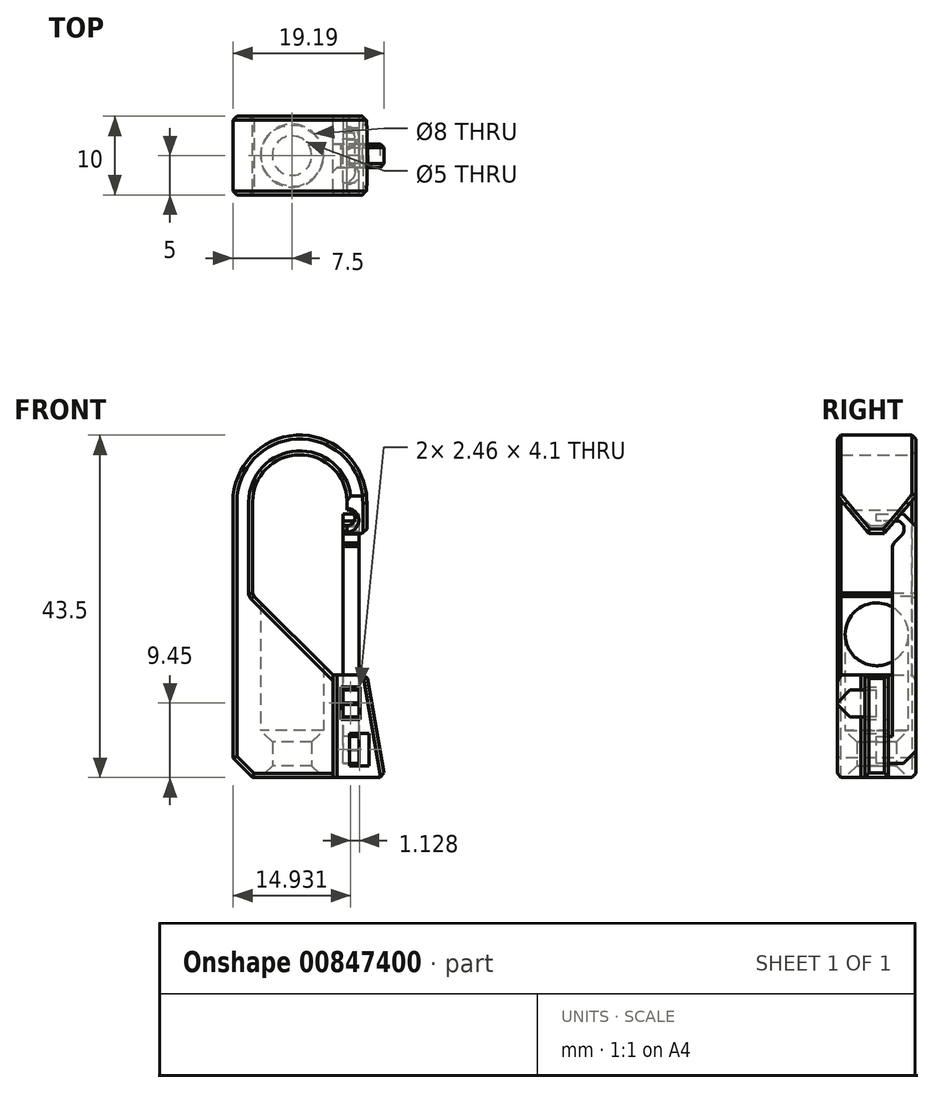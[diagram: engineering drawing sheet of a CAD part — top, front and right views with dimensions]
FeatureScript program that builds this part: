
annotation { "Feature Type Name" : "Feature", "Feature Type Description" : "" }
export const myFeature = defineFeature(function(context is Context, id is Id, definition is map)
    precondition{}
    {
        {
            var Q0;
            Q0=qCreatedBy(makeId("Top.planeOp"),FACE);
            var sketch = newSketch(context, id + "F0", { "sketchPlane" : qUnion([Q0])});
            skCircle(sketch, "E0", {"center": v(-1, -1.5) * mm, "radius": 4 * mm});
            skLineSegment(sketch, "E1.bottom", {"start": v(-8.5, 3.5) * mm, "end": v(8.5, 3.5) * mm});
            skLineSegment(sketch, "E1.top", {"start": v(-8.5, -6.5) * mm, "end": v(8.5, -6.5) * mm});
            skLineSegment(sketch, "E1.left", {"start": v(-8.5, 3.5) * mm, "end": v(-8.5, -6.5) * mm});
            skLineSegment(sketch, "E1.right", {"start": v(8.5, 3.5) * mm, "end": v(8.5, -6.5) * mm});
            skPoint(sketch, "E1.middle", {"position": v(0, -1.5) * mm});
            skCircle(sketch, "E2", {"center": v(-1, -1.5) * mm, "radius": 2.5 * mm});
            skSolve(sketch);
        }
        {
            var Q0;
            Q0=qCreatedBy(makeId("Front.planeOp"),FACE);
            cPlane(context, id + "F1", {"entities" : qUnion([Q0]), "cplaneType" : CPlaneType.OFFSET, "offset" : 3.5 * mm, "oppositeDirection" : true, "width" : 150 * mm, "height" : 150 * mm});
        }
        {
            var Q0;
            Q0=qCreatedBy(id+"F1.planeOp",FACE);
            var sketch = newSketch(context, id + "F2", { "sketchPlane" : qUnion([Q0])});
            skLineSegment(sketch, "E3", {"start": v(0, 0) * mm, "end": v(8.5, 0) * mm});
            skLineSegment(sketch, "E4.MirrorCS", {"start": v(0, 0) * mm, "end": v(-8.5, 0) * mm});
            skLineSegment(sketch, "E5", {"start": v(8.5, 0) * mm, "end": v(8.5, 13) * mm});
            skLineSegment(sketch, "E6", {"start": v(8.5, 13) * mm, "end": v(4.2, 13) * mm});
            skLineSegment(sketch, "E7", {"start": v(4.2, 13) * mm, "end": v(-6, 23.2) * mm});
            skLineSegment(sketch, "E8", {"start": v(-8.5, 0) * mm, "end": v(-8.5, 35) * mm});
            skLineSegment(sketch, "E9", {"start": v(-6, 23.2) * mm, "end": v(-6, 35) * mm});
            skLineSegment(sketch, "E10", {"start": v(-6, 35) * mm, "end": v(0, 35) * mm});
            skArc(sketch, "E11", {"start": v(8.5, 35) * mm, "mid": v(0, 43.5) * mm, "end": v(-8.5, 35) * mm});
            skArc(sketch, "E12", {"start": v(6, 35) * mm, "mid": v(0, 41) * mm, "end": v(-6, 35) * mm});
            skLineSegment(sketch, "E13", {"start": v(0, 35) * mm, "end": v(8.5, 35) * mm});
            skLineSegment(sketch, "E14", {"start": v(6, 35) * mm, "end": v(6, 31) * mm});
            skLineSegment(sketch, "E15.bottom", {"start": v(6, 31) * mm, "end": v(8.5, 31) * mm});
            skLineSegment(sketch, "E15.top", {"start": v(6, 35) * mm, "end": v(8.5, 35) * mm});
            skLineSegment(sketch, "E15.left", {"start": v(6, 31) * mm, "end": v(6, 35) * mm});
            skLineSegment(sketch, "E15.right", {"start": v(8.5, 31) * mm, "end": v(8.5, 35) * mm});
            skLineSegment(sketch, "E16", {"start": v(8.5, 13) * mm, "end": v(10.8, 0) * mm});
            skLineSegment(sketch, "E17", {"start": v(10.8, 0) * mm, "end": v(8.5, 0) * mm});
            skLineSegment(sketch, "E18", {"start": v(4.2, 13) * mm, "end": v(4.2, 0) * mm});
            skLineSegment(sketch, "E19.0", {"start": v(5.2, 12) * mm, "end": v(5.2, 0) * mm});
            skLineSegment(sketch, "E19.1", {"start": v(7.66, 12) * mm, "end": v(5.2, 12) * mm});
            skLineSegment(sketch, "E19.2", {"start": v(7.66, 12) * mm, "end": v(9.6, 1) * mm});
            skLineSegment(sketch, "E19.3", {"start": v(9.6, 1) * mm, "end": v(8.5, 1) * mm});
            skLineSegment(sketch, "E20", {"start": v(8.5, 1) * mm, "end": v(5.2, 1) * mm});
            skLineSegment(sketch, "E21", {"start": v(5.2, 12) * mm, "end": v(7.14, 1) * mm});
            skCircle(sketch, "E22", {"center": v(6, 33) * mm, "radius": 1 * mm});
            skLineSegment(sketch, "E23.0", {"start": v(8.5, 11.5) * mm, "end": v(4.2, 11.5) * mm});
            skLineSegment(sketch, "E24.0", {"start": v(0, 1.5) * mm, "end": v(8.5, 1.5) * mm});
            skLineSegment(sketch, "E24.1", {"start": v(10.8, 1.5) * mm, "end": v(8.5, 1.5) * mm});
            skLineSegment(sketch, "E25", {"start": v(8.79, 5.6) * mm, "end": v(8.79, 1) * mm});
            skLineSegment(sketch, "E26", {"start": v(8.79, 5.6) * mm, "end": v(6.33, 5.6) * mm});
            skLineSegment(sketch, "E27", {"start": v(7.66, 12) * mm, "end": v(7.66, 7.4) * mm});
            skLineSegment(sketch, "E28", {"start": v(7.66, 7.4) * mm, "end": v(5.2, 7.4) * mm});
            skLineSegment(sketch, "E29", {"start": v(6.33, 5.6) * mm, "end": v(6.33, 1) * mm});
            skSolve(sketch);
        }
        {
            var Q0;
            {var subQ1=sQuery(id+"F2.wireOp",EDGE,"E6");Q0=makeQuery(id+"F2.imprint","IMPRINT",FACE,{"disambiguationData":[TD([[makeQuery(id+"F2.imprint","IMPRINT",EDGE,{"derivedFrom":subQ1}),1.0]])]});}
            var Q1;
            {var subQ0=sQuery(id+"F2.wireOp",EDGE,"E23.0");var subQ1=sQuery(id+"F2.wireOp",EDGE,"E18");var subQ2=makeQuery(id+"F2.imprint","INTERSECT",VERTEX,{"derivedFrom":[subQ1,subQ0]});Q1=makeQuery(id+"F2.imprint","IMPRINT",FACE,{"disambiguationData":[TD([[makeQuery(id+"F2.imprint","IMPRINT",EDGE,{"disambiguationData":[TD([[subQ2,-1.0]])],"derivedFrom":subQ1}),1.0]])]});}
            var Q2;
            {var subQ4=sQuery(id+"F2.wireOp",EDGE,"E3");var subQ6=sQuery(id+"F2.wireOp",EDGE,"E18");var subQ7=makeQuery(id+"F2.imprint","INTERSECT",VERTEX,{"derivedFrom":[subQ4,subQ6]});Q2=makeQuery(id+"F2.imprint","IMPRINT",FACE,{"disambiguationData":[TD([[makeQuery(id+"F2.imprint","IMPRINT",EDGE,{"disambiguationData":[TD([[subQ7,-1.0]])],"derivedFrom":subQ4}),1.0]])]});}
            var Q3;
            {var subQ0=sQuery(id+"F2.wireOp",EDGE,"E19.0");var subQ1=sQuery(id+"F2.wireOp",EDGE,"E3");var subQ2=makeQuery(id+"F2.imprint","INTERSECT",VERTEX,{"derivedFrom":[subQ1,subQ0]});Q3=makeQuery(id+"F2.imprint","IMPRINT",FACE,{"disambiguationData":[TD([[makeQuery(id+"F2.imprint","IMPRINT",EDGE,{"disambiguationData":[TD([[subQ2,1.0]])],"derivedFrom":subQ0}),1.0]])]});}
            var Q4;
            {var subQ0=sQuery(id+"F2.wireOp",EDGE,"E17");Q4=makeQuery(id+"F2.imprint","IMPRINT",FACE,{"disambiguationData":[TD([[makeQuery(id+"F2.imprint","IMPRINT",EDGE,{"derivedFrom":subQ0}),-1.0]])]});}
            var Q5;
            {var subQ2=sQuery(id+"F2.wireOp",EDGE,"E5");var subQ6=makeQuery(id+"F2.imprint","INTERSECT",VERTEX,{"derivedFrom":[subQ2,sQuery(id+"F2.wireOp",EDGE,"E23.0")]});Q5=makeQuery(id+"F2.imprint","IMPRINT",FACE,{"disambiguationData":[TD([[makeQuery(id+"F2.imprint","IMPRINT",EDGE,{"disambiguationData":[TD([[subQ6,1.0]])],"derivedFrom":subQ2}),-1.0]])]});}
            var Q6;
            {var subQ4=sQuery(id+"F2.wireOp",EDGE,"E4.MirrorCS");Q6=makeQuery(id+"F2.imprint","IMPRINT",FACE,{"disambiguationData":[TD([[makeQuery(id+"F2.imprint","IMPRINT",EDGE,{"derivedFrom":subQ4}),-1.0]])]});}
            var Q7;
            {var subQ5=sQuery(id+"F2.wireOp",EDGE,"E5");var subQ7=sQuery(id+"F2.wireOp",EDGE,"E26");var subQ13=makeQuery(id+"F2.imprint","INTERSECT",VERTEX,{"derivedFrom":[subQ5,subQ7]});Q7=makeQuery(id+"F2.imprint","IMPRINT",FACE,{"disambiguationData":[TD([[makeQuery(id+"F2.imprint","IMPRINT",EDGE,{"disambiguationData":[TD([[subQ13,-1.0]])],"derivedFrom":subQ5}),1.0]])]});}
            var Q8;
            {var subQ1=sQuery(id+"F2.wireOp",EDGE,"E19.0");var subQ7=sQuery(id+"F2.wireOp",EDGE,"E28");var subQ9=makeQuery(id+"F2.imprint","INTERSECT",VERTEX,{"derivedFrom":[subQ1,subQ7]});Q8=makeQuery(id+"F2.imprint","IMPRINT",FACE,{"disambiguationData":[TD([[makeQuery(id+"F2.imprint","IMPRINT",EDGE,{"disambiguationData":[TD([[subQ9,-1.0]])],"derivedFrom":subQ1}),1.0]])]});}
            var Q9;
            {var subQ1=sQuery(id+"F2.wireOp",EDGE,"E19.2");var subQ3=sQuery(id+"F2.wireOp",EDGE,"E23.0");var subQ4=makeQuery(id+"F2.imprint","INTERSECT",VERTEX,{"derivedFrom":[subQ1,subQ3]});Q9=makeQuery(id+"F2.imprint","IMPRINT",FACE,{"disambiguationData":[TD([[makeQuery(id+"F2.imprint","IMPRINT",EDGE,{"disambiguationData":[TD([[subQ4,-1.0]])],"derivedFrom":subQ3}),-1.0]])]});}
            var Q10;
            {var subQ0=sQuery(id+"F2.wireOp",EDGE,"E23.0");var subQ1=sQuery(id+"F2.wireOp",EDGE,"E5");var subQ2=makeQuery(id+"F2.imprint","INTERSECT",VERTEX,{"derivedFrom":[subQ1,subQ0]});Q10=makeQuery(id+"F2.imprint","IMPRINT",FACE,{"disambiguationData":[TD([[makeQuery(id+"F2.imprint","IMPRINT",EDGE,{"disambiguationData":[TD([[subQ2,1.0]])],"derivedFrom":subQ1}),1.0]])]});}
            var Q11;
            {var subQ0=sQuery(id+"F2.wireOp",EDGE,"E20");var subQ1=sQuery(id+"F2.wireOp",EDGE,"E19.0");var subQ2=makeQuery(id+"F2.imprint","INTERSECT",VERTEX,{"derivedFrom":[subQ1,subQ0]});Q11=makeQuery(id+"F2.imprint","IMPRINT",FACE,{"disambiguationData":[TD([[makeQuery(id+"F2.imprint","IMPRINT",EDGE,{"disambiguationData":[TD([[subQ2,1.0]])],"derivedFrom":subQ1}),1.0]])]});}
            var Q12;
            {var subQ4=sQuery(id+"F2.wireOp",EDGE,"E15.bottom");Q12=makeQuery(id+"F2.imprint","IMPRINT",FACE,{"disambiguationData":[TD([[makeQuery(id+"F2.imprint","IMPRINT",EDGE,{"derivedFrom":subQ4}),1.0]])]});}
            var Q13;
            {var subQ0=sQuery(id+"F2.wireOp",EDGE,"UHZCBOe5-mY96-04BQ-GKVw-0XouIqEKjYRg");var subQ1=sQuery(id+"F2.wireOp",EDGE,"E15.right");var subQ2=makeQuery(id+"F2.imprint","INTERSECT",VERTEX,{"disambiguationData":[OD(0.0)],"derivedFrom":[subQ1,subQ0]});Q13=makeQuery(id+"F2.imprint","IMPRINT",FACE,{"disambiguationData":[TD([[makeQuery(id+"F2.imprint","IMPRINT",EDGE,{"disambiguationData":[TD([[subQ2,-1.0]])],"derivedFrom":subQ1}),1.0]])]});}
            var Q14;
            {var subQ1=sQuery(id+"F2.wireOp",EDGE,"E19.2");var subQ3=sQuery(id+"F2.wireOp",EDGE,"E24.1");var subQ4=makeQuery(id+"F2.imprint","INTERSECT",VERTEX,{"derivedFrom":[subQ1,subQ3]});Q14=makeQuery(id+"F2.imprint","IMPRINT",FACE,{"disambiguationData":[TD([[makeQuery(id+"F2.imprint","IMPRINT",EDGE,{"disambiguationData":[TD([[subQ4,-1.0]])],"derivedFrom":subQ3}),-1.0]])]});}
            var Q15;
            {var subQ0=sQuery(id+"F2.wireOp",EDGE,"E19.3");var subQ1=sQuery(id+"F2.wireOp",EDGE,"E19.2");var subQ2=makeQuery(id+"F2.imprint","INTERSECT",VERTEX,{"derivedFrom":[subQ1,subQ0]});Q15=makeQuery(id+"F2.imprint","IMPRINT",FACE,{"disambiguationData":[TD([[makeQuery(id+"F2.imprint","IMPRINT",EDGE,{"disambiguationData":[TD([[subQ2,1.0]])],"derivedFrom":subQ1}),-1.0]])]});}
            var Q16;
            {var subQ0=sQuery(id+"F2.wireOp",EDGE,"E26");var subQ1=sQuery(id+"F2.wireOp",EDGE,"E5");var subQ2=makeQuery(id+"F2.imprint","INTERSECT",VERTEX,{"derivedFrom":[subQ1,subQ0]});Q16=makeQuery(id+"F2.imprint","IMPRINT",FACE,{"disambiguationData":[TD([[makeQuery(id+"F2.imprint","IMPRINT",EDGE,{"disambiguationData":[TD([[subQ2,-1.0]])],"derivedFrom":subQ1}),-1.0]])]});}
            var Q17;
            {var subQ0=sQuery(id+"F2.wireOp",EDGE,"E21");var subQ1=sQuery(id+"F2.wireOp",EDGE,"E20");var subQ2=makeQuery(id+"F2.imprint","INTERSECT",VERTEX,{"derivedFrom":[subQ1,subQ0]});Q17=makeQuery(id+"F2.imprint","IMPRINT",FACE,{"disambiguationData":[TD([[makeQuery(id+"F2.imprint","IMPRINT",EDGE,{"disambiguationData":[TD([[subQ2,-1.0]])],"derivedFrom":subQ1}),-1.0]])]});}
            var Q18;
            {var subQ0=sQuery(id+"F2.wireOp",EDGE,"E20");var subQ5=sQuery(id+"F2.wireOp",EDGE,"E21");var subQ7=makeQuery(id+"F2.imprint","INTERSECT",VERTEX,{"derivedFrom":[subQ0,subQ5]});Q18=makeQuery(id+"F2.imprint","IMPRINT",FACE,{"disambiguationData":[TD([[makeQuery(id+"F2.imprint","IMPRINT",EDGE,{"disambiguationData":[TD([[subQ7,1.0]])],"derivedFrom":subQ5}),1.0]])]});}
            var Q19;
            {var subQ0=sQuery(id+"F2.wireOp",EDGE,"E19.3");var subQ5=sQuery(id+"F2.wireOp",EDGE,"E25");var subQ6=makeQuery(id+"F2.imprint","INTERSECT",VERTEX,{"derivedFrom":[subQ0,subQ5]});Q19=makeQuery(id+"F2.imprint","IMPRINT",FACE,{"disambiguationData":[TD([[makeQuery(id+"F2.imprint","IMPRINT",EDGE,{"disambiguationData":[TD([[subQ6,1.0]])],"derivedFrom":subQ5}),-1.0]])]});}
            var Q20;
            {var subQ0=sQuery(id+"F2.wireOp",EDGE,"E19.1");Q20=makeQuery(id+"F2.imprint","IMPRINT",FACE,{"disambiguationData":[TD([[makeQuery(id+"F2.imprint","IMPRINT",EDGE,{"derivedFrom":subQ0}),1.0]])]});}
            var Q21;
            {var subQ1=sQuery(id+"F2.wireOp",EDGE,"E19.0");var subQ3=sQuery(id+"F2.wireOp",EDGE,"E23.0");var subQ4=makeQuery(id+"F2.imprint","INTERSECT",VERTEX,{"derivedFrom":[subQ1,subQ3]});Q21=makeQuery(id+"F2.imprint","IMPRINT",FACE,{"disambiguationData":[TD([[makeQuery(id+"F2.imprint","IMPRINT",EDGE,{"disambiguationData":[TD([[subQ4,1.0]])],"derivedFrom":subQ3}),-1.0]])]});}
            var Q22;
            {var subQ1=sQuery(id+"F2.wireOp",EDGE,"E19.2");var subQ3=sQuery(id+"F2.wireOp",EDGE,"E23.0");var subQ4=makeQuery(id+"F2.imprint","INTERSECT",VERTEX,{"derivedFrom":[subQ1,subQ3]});Q22=makeQuery(id+"F2.imprint","IMPRINT",FACE,{"disambiguationData":[TD([[makeQuery(id+"F2.imprint","IMPRINT",EDGE,{"disambiguationData":[TD([[subQ4,-1.0]])],"derivedFrom":subQ3}),-1.0]])]});}
            extrude(context, id + "F3", {"entities" : qUnion([Q0, Q1, Q2, Q3, Q4, Q5, Q6, Q7, Q8, Q9, Q10, Q11, Q12, Q13, Q14, Q15, Q16, Q17, Q18, Q19, Q20, Q21, Q22]), "depth" : 10 * mm, "offsetDistance" : 25 * mm});
        }
        {
            var Q0;
            Q0=makeQuery(id+"F0.imprint","IMPRINT",FACE,{"disambiguationData":[TD([[makeQuery(id+"F0.imprint","IMPRINT",EDGE,{"derivedFrom":sQuery(id+"F0.wireOp",EDGE,"E0")}),1.0]])]});
            var Q1;
            Q1=makeQuery(id+"F0.imprint","IMPRINT",FACE,{"disambiguationData":[TD([[makeQuery(id+"F0.imprint","IMPRINT",EDGE,{"derivedFrom":sQuery(id+"F0.wireOp",EDGE,"E2")}),1.0]])]});
            extrude(context, id + "F4", {"entities" : qUnion([Q0, Q1]), "operationType" : NewBodyOperationType.REMOVE, "depth" : 25 * mm, "offsetDistance" : 25 * mm});
        }
        {
            var Q0;
            Q0=makeQuery(id+"F0.imprint","IMPRINT",FACE,{"disambiguationData":[TD([[makeQuery(id+"F0.imprint","IMPRINT",EDGE,{"derivedFrom":sQuery(id+"F0.wireOp",EDGE,"E0")}),1.0]])]});
            extrude(context, id + "F5", {"entities" : qUnion([Q0]), "operationType" : NewBodyOperationType.ADD, "depth" : 6 * mm, "offsetDistance" : 25 * mm});
        }
        {
            var Q0;
            Q0=makeQuery(id+"F3.opExtrude","CAP_EDGE",EDGE,{"disambiguationData":[OSD([sQuery(id+"F2.wireOp",EDGE,"E15.bottom")])],"isStart":false});
            var Q1;
            Q1=makeQuery(id+"F3.opExtrude","CAP_EDGE",EDGE,{"disambiguationData":[OSD([sQuery(id+"F2.wireOp",EDGE,"E15.bottom")])],"isStart":true});
            chamfer(context, id + "F6", {"entities" : qUnion([Q0, Q1]), "chamferType" : ChamferType.OFFSET_ANGLE, "width" : 4 * mm, "oppositeDirection" : true, "angle" : 50 * degree, "tangentPropagation" : true});
        }
        {
            var Q0;
            Q0=makeQuery(id+"F3.opExtrude","SWEPT_EDGE",EDGE,{"disambiguationData":[OSD([sQuery(id+"F2.wireOp",EDGE,"E4.MirrorCS"),sQuery(id+"F2.wireOp",EDGE,"E8")])]});
            chamfer(context, id + "F7", {"entities" : qUnion([Q0]), "width" : 2.5 * mm, "tangentPropagation" : true});
        }
        {
            var Q0;
            Q0=makeQuery(id+"F5.opExtrude","CAP_EDGE",EDGE,{"disambiguationData":[OSD([sQuery(id+"F0.wireOp",EDGE,"E2")])],"isStart":true});
            var Q1;
            Q1=makeQuery(id+"F5.opExtrude","CAP_EDGE",EDGE,{"disambiguationData":[OSD([sQuery(id+"F0.wireOp",EDGE,"E2")])],"isStart":false});
            chamfer(context, id + "F8", {"entities" : qUnion([Q0, Q1]), "width" : 1.5 * mm, "tangentPropagation" : true});
        }
        {
            var Q0;
            Q0=makeQuery(id+"F3.opExtrude","SWEPT_EDGE",EDGE,{"disambiguationData":[OSD([sQuery(id+"F2.wireOp",EDGE,"E7"),sQuery(id+"F2.wireOp",EDGE,"E9")])]});
            var Q1;
            Q1=makeQuery(id+"F3.opExtrude","SWEPT_EDGE",EDGE,{"disambiguationData":[OSD([sQuery(id+"F2.wireOp",EDGE,"E15.bottom"),sQuery(id+"F2.wireOp",EDGE,"E15.right")])]});
            chamfer(context, id + "F9", {"entities" : qUnion([Q0, Q1]), "width" : .6 * mm, "tangentPropagation" : true});
        }
        {
            var Q0;
            Q0=qCreatedBy(id+"F1.planeOp",FACE);
            var sketch = newSketch(context, id + "F10", { "sketchPlane" : qUnion([Q0])});
            skLineSegment(sketch, "E30", {"start": v(0, 0) * mm, "end": v(4.2, 0) * mm});
            skLineSegment(sketch, "E31", {"start": v(4.2, 0) * mm, "end": v(11.2, 0) * mm});
            skLineSegment(sketch, "E32", {"start": v(4.2, 0) * mm, "end": v(4.2, 15.17) * mm});
            skLineSegment(sketch, "E33.bottom", {"start": v(4.2, 15.17) * mm, "end": v(11.2, 15.17) * mm});
            skLineSegment(sketch, "E33.left", {"start": v(4.2, 15.17) * mm, "end": v(4.2, 0) * mm});
            skLineSegment(sketch, "E33.right", {"start": v(11.2, 15.17) * mm, "end": v(11.2, 0) * mm});
            skSolve(sketch);
        }
        {
            var Q0;
            Q0=qSketchRegion(id+"F10",true);
            extrude(context, id + "F11", {"entities" : qUnion([Q0]), "operationType" : NewBodyOperationType.REMOVE, "depth" : 3.5 * mm, "offsetDistance" : 25 * mm});
        }
        {
            var Q0;
            Q0=qCreatedBy(id+"F1.planeOp",FACE);
            cPlane(context, id + "F12", {"entities" : qUnion([Q0]), "cplaneType" : CPlaneType.OFFSET, "offset" : 10 * mm, "width" : 150 * mm, "height" : 150 * mm});
        }
        {
            var Q0;
            Q0=qCreatedBy(id+"F12.planeOp",FACE);
            var sketch = newSketch(context, id + "F13", { "sketchPlane" : qUnion([Q0])});
            skLineSegment(sketch, "E34", {"start": v(0, 0) * mm, "end": v(4.2, 0) * mm});
            skLineSegment(sketch, "E35", {"start": v(4.2, 0) * mm, "end": v(11.2, 0) * mm});
            skLineSegment(sketch, "E36", {"start": v(11.2, 0) * mm, "end": v(11.2, 14.54) * mm});
            skLineSegment(sketch, "E37.bottom", {"start": v(11.2, 14.54) * mm, "end": v(4.2, 14.54) * mm});
            skLineSegment(sketch, "E37.top", {"start": v(11.2, 0) * mm, "end": v(4.2, 0) * mm});
            skLineSegment(sketch, "E37.left", {"start": v(11.2, 14.54) * mm, "end": v(11.2, 0) * mm});
            skLineSegment(sketch, "E37.right", {"start": v(4.2, 14.54) * mm, "end": v(4.2, 0) * mm});
            skSolve(sketch);
        }
        {
            var Q0;
            Q0=qSketchRegion(id+"F13",true);
            extrude(context, id + "F14", {"entities" : qUnion([Q0]), "operationType" : NewBodyOperationType.REMOVE, "oppositeDirection" : true, "depth" : 3.5 * mm, "offsetDistance" : 25 * mm});
        }
        {
            var Q0;
            Q0=makeQuery(id+"F14.boolean.opBoolean","INTERSECT",EDGE,{"derivedFrom":[makeQuery(id+"F3.opExtrude","SWEPT_FACE",FACE,{"disambiguationData":[OSD([sQuery(id+"F2.wireOp",EDGE,"E16")])]}),makeQuery(id+"F14.opExtrude","CAP_FACE",FACE,{"disambiguationData":[OSD([sQuery(id+"F13.wireOp",EDGE,"E37.bottom"),sQuery(id+"F13.wireOp",EDGE,"E37.top"),sQuery(id+"F13.wireOp",EDGE,"E37.left"),sQuery(id+"F13.wireOp",EDGE,"E37.right")])],"isStart":false})]});
            var Q1;
            Q1=makeQuery(id+"F11.boolean.opBoolean","INTERSECT",EDGE,{"derivedFrom":[makeQuery(id+"F3.opExtrude","SWEPT_FACE",FACE,{"disambiguationData":[OSD([sQuery(id+"F2.wireOp",EDGE,"E16")])]}),makeQuery(id+"F11.opExtrude","CAP_FACE",FACE,{"disambiguationData":[OSD([sQuery(id+"F10.wireOp",EDGE,"E33.bottom"),sQuery(id+"F10.wireOp",EDGE,"E31"),sQuery(id+"F10.wireOp",EDGE,"E33.left"),sQuery(id+"F10.wireOp",EDGE,"E33.right")])],"isStart":false})]});
            var Q2;
            Q2=makeQuery(id+"F3.opExtrude","CAP_EDGE",EDGE,{"disambiguationData":[OSD([sQuery(id+"F2.wireOp",EDGE,"E8")])],"isStart":false});
            var Q3;
            Q3=makeQuery(id+"F3.opExtrude","CAP_EDGE",EDGE,{"disambiguationData":[OSD([sQuery(id+"F2.wireOp",EDGE,"E8")])],"isStart":true});
            var Q4;
            Q4=makeQuery(id+"F3.opExtrude","CAP_EDGE",EDGE,{"disambiguationData":[OSD([sQuery(id+"F2.wireOp",EDGE,"E9")])],"isStart":true});
            var Q5;
            Q5=makeQuery(id+"F3.opExtrude","CAP_EDGE",EDGE,{"disambiguationData":[OSD([sQuery(id+"F2.wireOp",EDGE,"E9")])],"isStart":false});
            var Q6;
            Q6=makeQuery(id+"F3.opExtrude","CAP_EDGE",EDGE,{"disambiguationData":[OSD([sQuery(id+"F2.wireOp",EDGE,"E7")])],"isStart":false});
            var Q7;
            Q7=makeQuery(id+"F3.opExtrude","CAP_EDGE",EDGE,{"disambiguationData":[OSD([sQuery(id+"F2.wireOp",EDGE,"E7")])],"isStart":true});
            var Q8;
            {var subQ0=sQuery(id+"F2.wireOp",EDGE,"E9");var subQ1=sQuery(id+"F2.wireOp",EDGE,"E7");Q8=makeQuery(id+"F9.opChamfer","BLEND_EDGE",EDGE,{"blendedFrom":[makeQuery(id+"F3.opExtrude","SWEPT_EDGE",EDGE,{"disambiguationData":[OSD([subQ1,subQ0])]}),makeQuery(id+"F3.opExtrude","CAP_FACE",FACE,{"disambiguationData":[OSD([sQuery(id+"F2.wireOp",EDGE,"E3"),sQuery(id+"F2.wireOp",EDGE,"E4.MirrorCS"),sQuery(id+"F2.wireOp",EDGE,"E6"),subQ1,sQuery(id+"F2.wireOp",EDGE,"E8"),subQ0,sQuery(id+"F2.wireOp",EDGE,"E11"),sQuery(id+"F2.wireOp",EDGE,"E12"),sQuery(id+"F2.wireOp",EDGE,"E15.bottom"),sQuery(id+"F2.wireOp",EDGE,"E15.left"),sQuery(id+"F2.wireOp",EDGE,"E15.right"),sQuery(id+"F2.wireOp",EDGE,"UHZCBOe5-mY96-04BQ-GKVw-0XouIqEKjYRg"),sQuery(id+"F2.wireOp",EDGE,"E16"),sQuery(id+"F2.wireOp",EDGE,"E17")])],"isStart":true})],"blendedInto":[makeQuery(id+"F3.opExtrude","CAP_FACE",FACE,{"disambiguationData":[OSD([sQuery(id+"F2.wireOp",EDGE,"E3"),sQuery(id+"F2.wireOp",EDGE,"E4.MirrorCS"),sQuery(id+"F2.wireOp",EDGE,"E6"),subQ1,sQuery(id+"F2.wireOp",EDGE,"E8"),subQ0,sQuery(id+"F2.wireOp",EDGE,"E11"),sQuery(id+"F2.wireOp",EDGE,"E12"),sQuery(id+"F2.wireOp",EDGE,"E15.bottom"),sQuery(id+"F2.wireOp",EDGE,"E15.left"),sQuery(id+"F2.wireOp",EDGE,"E15.right"),sQuery(id+"F2.wireOp",EDGE,"UHZCBOe5-mY96-04BQ-GKVw-0XouIqEKjYRg"),sQuery(id+"F2.wireOp",EDGE,"E16"),sQuery(id+"F2.wireOp",EDGE,"E17")])],"isStart":true})]});}
            var Q9;
            {var subQ0=sQuery(id+"F2.wireOp",EDGE,"E9");var subQ1=sQuery(id+"F2.wireOp",EDGE,"E7");Q9=makeQuery(id+"F9.opChamfer","BLEND_EDGE",EDGE,{"blendedFrom":[makeQuery(id+"F3.opExtrude","SWEPT_EDGE",EDGE,{"disambiguationData":[OSD([subQ1,subQ0])]}),makeQuery(id+"F3.opExtrude","CAP_FACE",FACE,{"disambiguationData":[OSD([sQuery(id+"F2.wireOp",EDGE,"E3"),sQuery(id+"F2.wireOp",EDGE,"E4.MirrorCS"),sQuery(id+"F2.wireOp",EDGE,"E6"),subQ1,sQuery(id+"F2.wireOp",EDGE,"E8"),subQ0,sQuery(id+"F2.wireOp",EDGE,"E11"),sQuery(id+"F2.wireOp",EDGE,"E12"),sQuery(id+"F2.wireOp",EDGE,"E15.bottom"),sQuery(id+"F2.wireOp",EDGE,"E15.left"),sQuery(id+"F2.wireOp",EDGE,"E15.right"),sQuery(id+"F2.wireOp",EDGE,"UHZCBOe5-mY96-04BQ-GKVw-0XouIqEKjYRg"),sQuery(id+"F2.wireOp",EDGE,"E16"),sQuery(id+"F2.wireOp",EDGE,"E17")])],"isStart":false})],"blendedInto":[makeQuery(id+"F3.opExtrude","CAP_FACE",FACE,{"disambiguationData":[OSD([sQuery(id+"F2.wireOp",EDGE,"E3"),sQuery(id+"F2.wireOp",EDGE,"E4.MirrorCS"),sQuery(id+"F2.wireOp",EDGE,"E6"),subQ1,sQuery(id+"F2.wireOp",EDGE,"E8"),subQ0,sQuery(id+"F2.wireOp",EDGE,"E11"),sQuery(id+"F2.wireOp",EDGE,"E12"),sQuery(id+"F2.wireOp",EDGE,"E15.bottom"),sQuery(id+"F2.wireOp",EDGE,"E15.left"),sQuery(id+"F2.wireOp",EDGE,"E15.right"),sQuery(id+"F2.wireOp",EDGE,"UHZCBOe5-mY96-04BQ-GKVw-0XouIqEKjYRg"),sQuery(id+"F2.wireOp",EDGE,"E16"),sQuery(id+"F2.wireOp",EDGE,"E17")])],"isStart":false})]});}
            var Q10;
            Q10=makeQuery(id+"F6.opChamfer","BLEND_EDGE",EDGE,{"blendedFrom":[makeQuery(id+"F3.opExtrude","CAP_EDGE",EDGE,{"disambiguationData":[OSD([sQuery(id+"F2.wireOp",EDGE,"E15.bottom")])],"isStart":false}),makeQuery(id+"F3.opExtrude","SWEPT_FACE",FACE,{"disambiguationData":[OSD([sQuery(id+"F2.wireOp",EDGE,"E15.left")])]})],"blendedInto":[makeQuery(id+"F3.opExtrude","SWEPT_FACE",FACE,{"disambiguationData":[OSD([sQuery(id+"F2.wireOp",EDGE,"E15.left")])]})]});
            var Q11;
            Q11=makeQuery(id+"F6.opChamfer","BLEND_EDGE",EDGE,{"blendedFrom":[makeQuery(id+"F3.opExtrude","CAP_EDGE",EDGE,{"disambiguationData":[OSD([sQuery(id+"F2.wireOp",EDGE,"E15.bottom")])],"isStart":true}),makeQuery(id+"F3.opExtrude","SWEPT_FACE",FACE,{"disambiguationData":[OSD([sQuery(id+"F2.wireOp",EDGE,"E15.left")])]})],"blendedInto":[makeQuery(id+"F3.opExtrude","SWEPT_FACE",FACE,{"disambiguationData":[OSD([sQuery(id+"F2.wireOp",EDGE,"E15.left")])]})]});
            var Q12;
            {var subQ0=sQuery(id+"F2.wireOp",EDGE,"E15.right");Q12=makeQuery(id+"F6.opChamfer","BLEND_EDGE",EDGE,{"blendedFrom":[makeQuery(id+"F3.opExtrude","CAP_EDGE",EDGE,{"disambiguationData":[OSD([sQuery(id+"F2.wireOp",EDGE,"E15.bottom")])],"isStart":false}),makeQuery(id+"F3.opExtrude","SWEPT_FACE",FACE,{"disambiguationData":[OSD([subQ0]),TDD([makeQuery(id+"F2.imprint","IMPRINT",EDGE,{"disambiguationData":[TD([[makeQuery(id+"F2.imprint","INTERSECT",VERTEX,{"disambiguationData":[OD(1.0)],"derivedFrom":[subQ0,sQuery(id+"F2.wireOp",EDGE,"UHZCBOe5-mY96-04BQ-GKVw-0XouIqEKjYRg")]}),-1.0]])],"derivedFrom":subQ0})])]})],"blendedInto":[makeQuery(id+"F3.opExtrude","SWEPT_FACE",FACE,{"disambiguationData":[OSD([subQ0]),TDD([makeQuery(id+"F2.imprint","IMPRINT",EDGE,{"disambiguationData":[TD([[makeQuery(id+"F2.imprint","INTERSECT",VERTEX,{"disambiguationData":[OD(1.0)],"derivedFrom":[subQ0,sQuery(id+"F2.wireOp",EDGE,"UHZCBOe5-mY96-04BQ-GKVw-0XouIqEKjYRg")]}),-1.0]])],"derivedFrom":subQ0})])]})]});}
            var Q13;
            Q13=makeQuery(id+"F6.opChamfer","BLEND_EDGE",EDGE,{"blendedFrom":[makeQuery(id+"F3.opExtrude","CAP_EDGE",EDGE,{"disambiguationData":[OSD([sQuery(id+"F2.wireOp",EDGE,"E15.bottom")])],"isStart":false}),makeQuery(id+"F3.opExtrude","SWEPT_FACE",FACE,{"disambiguationData":[OSD([sQuery(id+"F2.wireOp",EDGE,"UHZCBOe5-mY96-04BQ-GKVw-0XouIqEKjYRg")])]})],"blendedInto":[makeQuery(id+"F3.opExtrude","SWEPT_FACE",FACE,{"disambiguationData":[OSD([sQuery(id+"F2.wireOp",EDGE,"UHZCBOe5-mY96-04BQ-GKVw-0XouIqEKjYRg")])]})]});
            var Q14;
            {var subQ0=sQuery(id+"F2.wireOp",EDGE,"E15.right");var subQ1=sQuery(id+"F2.wireOp",EDGE,"E15.bottom");Q14=makeQuery(id+"F6.opChamfer","BLEND_EDGE",EDGE,{"blendedFrom":[makeQuery(id+"F3.opExtrude","CAP_EDGE",EDGE,{"disambiguationData":[OSD([subQ1])],"isStart":false}),makeQuery(id+"F3.opExtrude","SWEPT_FACE",FACE,{"disambiguationData":[OSD([subQ0]),TDD([makeQuery(id+"F2.imprint","IMPRINT",EDGE,{"disambiguationData":[TD([[makeQuery(id+"F2.imprint","INTERSECT",VERTEX,{"derivedFrom":[subQ1,subQ0]}),-1.0]])],"derivedFrom":subQ0})])]})],"blendedInto":[makeQuery(id+"F3.opExtrude","SWEPT_FACE",FACE,{"disambiguationData":[OSD([subQ0]),TDD([makeQuery(id+"F2.imprint","IMPRINT",EDGE,{"disambiguationData":[TD([[makeQuery(id+"F2.imprint","INTERSECT",VERTEX,{"derivedFrom":[subQ1,subQ0]}),-1.0]])],"derivedFrom":subQ0})])]})]});}
            var Q15;
            {var subQ0=sQuery(id+"F2.wireOp",EDGE,"E15.right");Q15=makeQuery(id+"F6.opChamfer","BLEND_EDGE",EDGE,{"blendedFrom":[makeQuery(id+"F3.opExtrude","CAP_EDGE",EDGE,{"disambiguationData":[OSD([sQuery(id+"F2.wireOp",EDGE,"E15.bottom")])],"isStart":true}),makeQuery(id+"F3.opExtrude","SWEPT_FACE",FACE,{"disambiguationData":[OSD([subQ0]),TDD([makeQuery(id+"F2.imprint","IMPRINT",EDGE,{"disambiguationData":[TD([[makeQuery(id+"F2.imprint","INTERSECT",VERTEX,{"disambiguationData":[OD(1.0)],"derivedFrom":[subQ0,sQuery(id+"F2.wireOp",EDGE,"UHZCBOe5-mY96-04BQ-GKVw-0XouIqEKjYRg")]}),-1.0]])],"derivedFrom":subQ0})])]})],"blendedInto":[makeQuery(id+"F3.opExtrude","SWEPT_FACE",FACE,{"disambiguationData":[OSD([subQ0]),TDD([makeQuery(id+"F2.imprint","IMPRINT",EDGE,{"disambiguationData":[TD([[makeQuery(id+"F2.imprint","INTERSECT",VERTEX,{"disambiguationData":[OD(1.0)],"derivedFrom":[subQ0,sQuery(id+"F2.wireOp",EDGE,"UHZCBOe5-mY96-04BQ-GKVw-0XouIqEKjYRg")]}),-1.0]])],"derivedFrom":subQ0})])]})]});}
            var Q16;
            Q16=makeQuery(id+"F6.opChamfer","BLEND_EDGE",EDGE,{"blendedFrom":[makeQuery(id+"F3.opExtrude","CAP_EDGE",EDGE,{"disambiguationData":[OSD([sQuery(id+"F2.wireOp",EDGE,"E15.bottom")])],"isStart":true}),makeQuery(id+"F3.opExtrude","SWEPT_FACE",FACE,{"disambiguationData":[OSD([sQuery(id+"F2.wireOp",EDGE,"UHZCBOe5-mY96-04BQ-GKVw-0XouIqEKjYRg")])]})],"blendedInto":[makeQuery(id+"F3.opExtrude","SWEPT_FACE",FACE,{"disambiguationData":[OSD([sQuery(id+"F2.wireOp",EDGE,"UHZCBOe5-mY96-04BQ-GKVw-0XouIqEKjYRg")])]})]});
            var Q17;
            {var subQ0=sQuery(id+"F2.wireOp",EDGE,"E15.right");var subQ1=sQuery(id+"F2.wireOp",EDGE,"E15.bottom");Q17=makeQuery(id+"F6.opChamfer","BLEND_EDGE",EDGE,{"blendedFrom":[makeQuery(id+"F3.opExtrude","CAP_EDGE",EDGE,{"disambiguationData":[OSD([subQ1])],"isStart":true}),makeQuery(id+"F3.opExtrude","SWEPT_FACE",FACE,{"disambiguationData":[OSD([subQ0]),TDD([makeQuery(id+"F2.imprint","IMPRINT",EDGE,{"disambiguationData":[TD([[makeQuery(id+"F2.imprint","INTERSECT",VERTEX,{"derivedFrom":[subQ1,subQ0]}),-1.0]])],"derivedFrom":subQ0})])]})],"blendedInto":[makeQuery(id+"F3.opExtrude","SWEPT_FACE",FACE,{"disambiguationData":[OSD([subQ0]),TDD([makeQuery(id+"F2.imprint","IMPRINT",EDGE,{"disambiguationData":[TD([[makeQuery(id+"F2.imprint","INTERSECT",VERTEX,{"derivedFrom":[subQ1,subQ0]}),-1.0]])],"derivedFrom":subQ0})])]})]});}
            var Q18;
            Q18=makeQuery(id+"F11.boolean.opBoolean","COPY",EDGE,{"derivedFrom":makeQuery(id+"F11.opExtrude","CAP_EDGE",EDGE,{"disambiguationData":[OSD([sQuery(id+"F10.wireOp",EDGE,"E33.left")])],"isStart":true})});
            var Q19;
            Q19=makeQuery(id+"F14.boolean.opBoolean","COPY",EDGE,{"derivedFrom":makeQuery(id+"F14.opExtrude","CAP_EDGE",EDGE,{"disambiguationData":[OSD([sQuery(id+"F13.wireOp",EDGE,"E37.right")])],"isStart":true})});
            var Q20;
            Q20=makeQuery(id+"F14.boolean.opBoolean","COPY",EDGE,{"derivedFrom":makeQuery(id+"F14.opExtrude","CAP_EDGE",EDGE,{"disambiguationData":[OSD([sQuery(id+"F13.wireOp",EDGE,"E37.right")])],"isStart":false})});
            var Q21;
            Q21=makeQuery(id+"F11.boolean.opBoolean","COPY",EDGE,{"derivedFrom":makeQuery(id+"F11.opExtrude","CAP_EDGE",EDGE,{"disambiguationData":[OSD([sQuery(id+"F10.wireOp",EDGE,"E33.left")])],"isStart":false})});
            var Q22;
            Q22=makeQuery(id+"F3.opExtrude","SWEPT_EDGE",EDGE,{"disambiguationData":[OSD([sQuery(id+"F2.wireOp",EDGE,"E5"),sQuery(id+"F2.wireOp",EDGE,"E6"),sQuery(id+"F2.wireOp",EDGE,"E16")])]});
            var Q23;
            Q23=makeQuery(id+"F3.opExtrude","CAP_EDGE",EDGE,{"disambiguationData":[OSD([sQuery(id+"F2.wireOp",EDGE,"E3"),sQuery(id+"F2.wireOp",EDGE,"E4.MirrorCS"),sQuery(id+"F2.wireOp",EDGE,"E17")])],"isStart":false});
            var Q24;
            Q24=makeQuery(id+"F3.opExtrude","CAP_EDGE",EDGE,{"disambiguationData":[OSD([sQuery(id+"F2.wireOp",EDGE,"E3"),sQuery(id+"F2.wireOp",EDGE,"E4.MirrorCS"),sQuery(id+"F2.wireOp",EDGE,"E17")])],"isStart":true});
            var Q25;
            Q25=makeQuery(id+"F3.opExtrude","SWEPT_EDGE",EDGE,{"disambiguationData":[OSD([sQuery(id+"F2.wireOp",EDGE,"E4.MirrorCS"),sQuery(id+"F2.wireOp",EDGE,"E8")])]});
            var Q26;
            Q26=makeQuery(id+"F3.opExtrude","SWEPT_EDGE",EDGE,{"disambiguationData":[OSD([sQuery(id+"F2.wireOp",EDGE,"E16"),sQuery(id+"F2.wireOp",EDGE,"E17")])]});
            var Q27;
            Q27=makeQuery(id+"F6.opChamfer","BLEND_EDGE",EDGE,{"blendedFrom":[makeQuery(id+"F3.opExtrude","CAP_EDGE",EDGE,{"disambiguationData":[OSD([sQuery(id+"F2.wireOp",EDGE,"E15.bottom")])],"isStart":false}),makeQuery(id+"F3.opExtrude","SWEPT_FACE",FACE,{"disambiguationData":[OSD([sQuery(id+"F2.wireOp",EDGE,"E22")])]})],"blendedInto":[makeQuery(id+"F3.opExtrude","SWEPT_FACE",FACE,{"disambiguationData":[OSD([sQuery(id+"F2.wireOp",EDGE,"E22")])]})]});
            var Q28;
            Q28=makeQuery(id+"F6.opChamfer","BLEND_EDGE",EDGE,{"blendedFrom":[makeQuery(id+"F3.opExtrude","CAP_EDGE",EDGE,{"disambiguationData":[OSD([sQuery(id+"F2.wireOp",EDGE,"E15.bottom")])],"isStart":true}),makeQuery(id+"F3.opExtrude","SWEPT_FACE",FACE,{"disambiguationData":[OSD([sQuery(id+"F2.wireOp",EDGE,"E22")])]})],"blendedInto":[makeQuery(id+"F3.opExtrude","SWEPT_FACE",FACE,{"disambiguationData":[OSD([sQuery(id+"F2.wireOp",EDGE,"E22")])]})]});
            var Q29;
            {var subQ0=sQuery(id+"F2.wireOp",EDGE,"E8");var subQ1=sQuery(id+"F2.wireOp",EDGE,"E4.MirrorCS");Q29=makeQuery(id+"F7.opChamfer","BLEND_EDGE",EDGE,{"blendedFrom":[makeQuery(id+"F3.opExtrude","SWEPT_EDGE",EDGE,{"disambiguationData":[OSD([subQ1,subQ0])]}),makeQuery(id+"F3.opExtrude","CAP_FACE",FACE,{"disambiguationData":[OSD([sQuery(id+"F2.wireOp",EDGE,"E3"),subQ1,sQuery(id+"F2.wireOp",EDGE,"E6"),sQuery(id+"F2.wireOp",EDGE,"E7"),subQ0,sQuery(id+"F2.wireOp",EDGE,"E9"),sQuery(id+"F2.wireOp",EDGE,"E11"),sQuery(id+"F2.wireOp",EDGE,"E12"),sQuery(id+"F2.wireOp",EDGE,"E15.bottom"),sQuery(id+"F2.wireOp",EDGE,"E15.left"),sQuery(id+"F2.wireOp",EDGE,"E15.right"),sQuery(id+"F2.wireOp",EDGE,"E16"),sQuery(id+"F2.wireOp",EDGE,"E17"),sQuery(id+"F2.wireOp",EDGE,"E19.0"),sQuery(id+"F2.wireOp",EDGE,"E22"),sQuery(id+"F2.wireOp",EDGE,"E23.0"),sQuery(id+"F2.wireOp",EDGE,"E24.0"),sQuery(id+"F2.wireOp",EDGE,"E24.1"),sQuery(id+"F2.wireOp",EDGE,"E25"),sQuery(id+"F2.wireOp",EDGE,"E26"),sQuery(id+"F2.wireOp",EDGE,"E27"),sQuery(id+"F2.wireOp",EDGE,"E28"),sQuery(id+"F2.wireOp",EDGE,"E29")])],"isStart":false})],"blendedInto":[makeQuery(id+"F3.opExtrude","CAP_FACE",FACE,{"disambiguationData":[OSD([sQuery(id+"F2.wireOp",EDGE,"E3"),subQ1,sQuery(id+"F2.wireOp",EDGE,"E6"),sQuery(id+"F2.wireOp",EDGE,"E7"),subQ0,sQuery(id+"F2.wireOp",EDGE,"E9"),sQuery(id+"F2.wireOp",EDGE,"E11"),sQuery(id+"F2.wireOp",EDGE,"E12"),sQuery(id+"F2.wireOp",EDGE,"E15.bottom"),sQuery(id+"F2.wireOp",EDGE,"E15.left"),sQuery(id+"F2.wireOp",EDGE,"E15.right"),sQuery(id+"F2.wireOp",EDGE,"E16"),sQuery(id+"F2.wireOp",EDGE,"E17"),sQuery(id+"F2.wireOp",EDGE,"E19.0"),sQuery(id+"F2.wireOp",EDGE,"E22"),sQuery(id+"F2.wireOp",EDGE,"E23.0"),sQuery(id+"F2.wireOp",EDGE,"E24.0"),sQuery(id+"F2.wireOp",EDGE,"E24.1"),sQuery(id+"F2.wireOp",EDGE,"E25"),sQuery(id+"F2.wireOp",EDGE,"E26"),sQuery(id+"F2.wireOp",EDGE,"E27"),sQuery(id+"F2.wireOp",EDGE,"E28"),sQuery(id+"F2.wireOp",EDGE,"E29")])],"isStart":false})]});}
            var Q30;
            {var subQ0=sQuery(id+"F2.wireOp",EDGE,"E8");var subQ1=sQuery(id+"F2.wireOp",EDGE,"E4.MirrorCS");Q30=makeQuery(id+"F7.opChamfer","BLEND_EDGE",EDGE,{"blendedFrom":[makeQuery(id+"F3.opExtrude","SWEPT_EDGE",EDGE,{"disambiguationData":[OSD([subQ1,subQ0])]}),makeQuery(id+"F3.opExtrude","CAP_FACE",FACE,{"disambiguationData":[OSD([sQuery(id+"F2.wireOp",EDGE,"E3"),subQ1,sQuery(id+"F2.wireOp",EDGE,"E6"),sQuery(id+"F2.wireOp",EDGE,"E7"),subQ0,sQuery(id+"F2.wireOp",EDGE,"E9"),sQuery(id+"F2.wireOp",EDGE,"E11"),sQuery(id+"F2.wireOp",EDGE,"E12"),sQuery(id+"F2.wireOp",EDGE,"E15.bottom"),sQuery(id+"F2.wireOp",EDGE,"E15.left"),sQuery(id+"F2.wireOp",EDGE,"E15.right"),sQuery(id+"F2.wireOp",EDGE,"E16"),sQuery(id+"F2.wireOp",EDGE,"E17"),sQuery(id+"F2.wireOp",EDGE,"E19.0"),sQuery(id+"F2.wireOp",EDGE,"E22"),sQuery(id+"F2.wireOp",EDGE,"E23.0"),sQuery(id+"F2.wireOp",EDGE,"E24.0"),sQuery(id+"F2.wireOp",EDGE,"E24.1"),sQuery(id+"F2.wireOp",EDGE,"E25"),sQuery(id+"F2.wireOp",EDGE,"E26"),sQuery(id+"F2.wireOp",EDGE,"E27"),sQuery(id+"F2.wireOp",EDGE,"E28"),sQuery(id+"F2.wireOp",EDGE,"E29")])],"isStart":true})],"blendedInto":[makeQuery(id+"F3.opExtrude","CAP_FACE",FACE,{"disambiguationData":[OSD([sQuery(id+"F2.wireOp",EDGE,"E3"),subQ1,sQuery(id+"F2.wireOp",EDGE,"E6"),sQuery(id+"F2.wireOp",EDGE,"E7"),subQ0,sQuery(id+"F2.wireOp",EDGE,"E9"),sQuery(id+"F2.wireOp",EDGE,"E11"),sQuery(id+"F2.wireOp",EDGE,"E12"),sQuery(id+"F2.wireOp",EDGE,"E15.bottom"),sQuery(id+"F2.wireOp",EDGE,"E15.left"),sQuery(id+"F2.wireOp",EDGE,"E15.right"),sQuery(id+"F2.wireOp",EDGE,"E16"),sQuery(id+"F2.wireOp",EDGE,"E17"),sQuery(id+"F2.wireOp",EDGE,"E19.0"),sQuery(id+"F2.wireOp",EDGE,"E22"),sQuery(id+"F2.wireOp",EDGE,"E23.0"),sQuery(id+"F2.wireOp",EDGE,"E24.0"),sQuery(id+"F2.wireOp",EDGE,"E24.1"),sQuery(id+"F2.wireOp",EDGE,"E25"),sQuery(id+"F2.wireOp",EDGE,"E26"),sQuery(id+"F2.wireOp",EDGE,"E27"),sQuery(id+"F2.wireOp",EDGE,"E28"),sQuery(id+"F2.wireOp",EDGE,"E29")])],"isStart":true})]});}
            chamfer(context, id + "F15", {"entities" : qUnion([Q0, Q1, Q2, Q3, Q4, Q5, Q6, Q7, Q8, Q9, Q10, Q11, Q12, Q13, Q14, Q15, Q16, Q17, Q18, Q19, Q20, Q21, Q22, Q23, Q24, Q25, Q26, Q27, Q28, Q29, Q30]), "width" : .5 * mm, "tangentPropagation" : true});
        }
        {
            var Q0;
            Q0=qCreatedBy(makeId("Right.planeOp"),FACE);
            cPlane(context, id + "F16", {"entities" : qUnion([Q0]), "cplaneType" : CPlaneType.OFFSET, "offset" : 5.5 * mm, "width" : 150 * mm, "height" : 150 * mm});
        }
        {
            var Q0;
            Q0=qCreatedBy(id+"F16.planeOp",FACE);
            var sketch = newSketch(context, id + "F17", { "sketchPlane" : qUnion([Q0])});
            skLineSegment(sketch, "E38", {"start": v(0, 0) * mm, "end": v(-1.5, 0) * mm});
            skLineSegment(sketch, "E39", {"start": v(-1.5, 0) * mm, "end": v(-1.5, 33.5) * mm});
            skLineSegment(sketch, "E40", {"start": v(-1.5, 33.5) * mm, "end": v(3.5, 33.5) * mm});
            skLineSegment(sketch, "E41", {"start": v(3.5, 33.5) * mm, "end": v(3.5, 0) * mm});
            skLineSegment(sketch, "E42", {"start": v(3.5, 0) * mm, "end": v(-1.5, 0) * mm});
            skLineSegment(sketch, "E43", {"start": v(-1.5, 0) * mm, "end": v(-1.5, 5.2) * mm});
            skLineSegment(sketch, "E44", {"start": v(-1.5, 5.2) * mm, "end": v(0.5, 5.2) * mm});
            skLineSegment(sketch, "E45", {"start": v(0.5, 5.2) * mm, "end": v(0.5, 32.6) * mm});
            skLineSegment(sketch, "E46", {"start": v(0.5, 32.6) * mm, "end": v(-1.5, 32.6) * mm});
            skLineSegment(sketch, "E47.MirrorCS", {"start": v(-3.5, 32.6) * mm, "end": v(-1.5, 32.6) * mm});
            skLineSegment(sketch, "E48.MirrorCS", {"start": v(-1.5, 33.5) * mm, "end": v(-6.5, 33.5) * mm});
            skLineSegment(sketch, "E49.MirrorCS", {"start": v(-6.5, 33.5) * mm, "end": v(-6.5, 0) * mm});
            skLineSegment(sketch, "E50", {"start": v(-6.5, 0) * mm, "end": v(-6.5, 11.1) * mm});
            skLineSegment(sketch, "E51", {"start": v(-6.5, 11.1) * mm, "end": v(-1.5, 11.1) * mm});
            skLineSegment(sketch, "E52", {"start": v(-1.5, 11.1) * mm, "end": v(-1.5, 7.7) * mm});
            skLineSegment(sketch, "E53", {"start": v(-1.5, 7.7) * mm, "end": v(-6.5, 7.7) * mm});
            skLineSegment(sketch, "E54", {"start": v(-3.5, 32.6) * mm, "end": v(-3.5, 11.1) * mm});
            skPoint(sketch, "E54.endSnap0", {"position": v(-4, 11.1) * mm});
            skLineSegment(sketch, "E55", {"start": v(3.5, 0) * mm, "end": v(3.5, 1.8) * mm});
            skLineSegment(sketch, "E56", {"start": v(3.5, 1.8) * mm, "end": v(-1.5, 1.8) * mm});
            skLineSegment(sketch, "E57", {"start": v(-1.5, 5.2) * mm, "end": v(-2.5, 5.2) * mm});
            skLineSegment(sketch, "E58.bottom", {"start": v(-2.5, 5.2) * mm, "end": v(-1.5, 5.2) * mm});
            skLineSegment(sketch, "E58.top", {"start": v(-2.5, 1.8) * mm, "end": v(-1.5, 1.8) * mm});
            skLineSegment(sketch, "E58.left", {"start": v(-2.5, 5.2) * mm, "end": v(-2.5, 1.8) * mm});
            skLineSegment(sketch, "E58.right", {"start": v(-1.5, 5.2) * mm, "end": v(-1.5, 1.8) * mm});
            skLineSegment(sketch, "E59", {"start": v(-1.5, 7.7) * mm, "end": v(-0.5, 7.7) * mm});
            skLineSegment(sketch, "E60.bottom", {"start": v(-0.5, 7.7) * mm, "end": v(-1.5, 7.7) * mm});
            skLineSegment(sketch, "E60.top", {"start": v(-0.5, 11.1) * mm, "end": v(-1.5, 11.1) * mm});
            skLineSegment(sketch, "E60.left", {"start": v(-0.5, 7.7) * mm, "end": v(-0.5, 11.1) * mm});
            skLineSegment(sketch, "E60.right", {"start": v(-1.5, 7.7) * mm, "end": v(-1.5, 11.1) * mm});
            skLineSegment(sketch, "E61", {"start": v(0.5, 32.6) * mm, "end": v(2, 32.6) * mm});
            skLineSegment(sketch, "E62", {"start": v(2, 32.6) * mm, "end": v(2, 31.1) * mm});
            skLineSegment(sketch, "E63", {"start": v(2, 31.1) * mm, "end": v(0.5, 29.6) * mm});
            skLineSegment(sketch, "E64.MirrorCS", {"start": v(-3.5, 32.6) * mm, "end": v(-5, 32.6) * mm});
            skLineSegment(sketch, "E65.MirrorCS", {"start": v(-5, 32.6) * mm, "end": v(-5, 31.1) * mm});
            skLineSegment(sketch, "E66.MirrorCS", {"start": v(-5, 31.1) * mm, "end": v(-3.5, 29.6) * mm});
            skSolve(sketch);
        }
        {
            var Q0;
            {var subQ0=sQuery(id+"F17.wireOp",EDGE,"E49.MirrorCS");Q0=makeQuery(id+"F17.imprint","IMPRINT",FACE,{"disambiguationData":[TD([[makeQuery(id+"F17.imprint","IMPRINT",EDGE,{"derivedFrom":subQ0}),1.0]])]});}
            var Q1;
            {var subQ0=sQuery(id+"F17.wireOp",EDGE,"E52");Q1=makeQuery(id+"F17.imprint","IMPRINT",FACE,{"disambiguationData":[TD([[makeQuery(id+"F17.imprint","IMPRINT",EDGE,{"derivedFrom":subQ0}),-1.0]])]});}
            var Q2;
            Q2=makeQuery(id+"F17.imprint","IMPRINT",FACE,{"disambiguationData":[TD([[makeQuery(id+"F17.imprint","IMPRINT",EDGE,{"derivedFrom":sQuery(id+"F17.wireOp",EDGE,"E40")}),-1.0]])]});
            var Q3;
            {var subQ0=sQuery(id+"F17.wireOp",EDGE,"E53");Q3=makeQuery(id+"F17.imprint","IMPRINT",FACE,{"disambiguationData":[TD([[makeQuery(id+"F17.imprint","IMPRINT",EDGE,{"derivedFrom":subQ0}),-1.0]])]});}
            var Q4;
            Q4=makeQuery(id+"F17.imprint","IMPRINT",FACE,{"disambiguationData":[TD([[makeQuery(id+"F17.imprint","IMPRINT",EDGE,{"derivedFrom":sQuery(id+"F17.wireOp",EDGE,"E58.bottom")}),-1.0]])]});
            var Q5;
            Q5=makeQuery(id+"F17.imprint","IMPRINT",FACE,{"disambiguationData":[TD([[makeQuery(id+"F17.imprint","IMPRINT",EDGE,{"derivedFrom":sQuery(id+"F17.wireOp",EDGE,"E60.bottom")}),-1.0]])]});
            extrude(context, id + "F18", {"entities" : qUnion([Q0, Q1, Q2, Q3, Q4, Q5]), "depth" : 2 * mm, "offsetDistance" : 25 * mm});
        }
        {
            var Q0;
            Q0=makeQuery(id+"F18.opExtrude","SWEPT_EDGE",EDGE,{"disambiguationData":[OSD([sQuery(id+"F17.wireOp",EDGE,"E48.MirrorCS"),sQuery(id+"F17.wireOp",EDGE,"E49.MirrorCS")])]});
            var Q1;
            Q1=makeQuery(id+"F18.opExtrude","SWEPT_EDGE",EDGE,{"disambiguationData":[OSD([sQuery(id+"F17.wireOp",EDGE,"E40"),sQuery(id+"F17.wireOp",EDGE,"E41")])]});
            var Q2;
            Q2=makeQuery(id+"F18.opExtrude","SWEPT_EDGE",EDGE,{"disambiguationData":[OSD([sQuery(id+"F17.wireOp",EDGE,"E50"),sQuery(id+"F17.wireOp",EDGE,"E53")])]});
            var Q3;
            Q3=makeQuery(id+"F18.opExtrude","SWEPT_EDGE",EDGE,{"disambiguationData":[OSD([sQuery(id+"F17.wireOp",EDGE,"E41"),sQuery(id+"F17.wireOp",EDGE,"E55"),sQuery(id+"F17.wireOp",EDGE,"E56")])]});
            chamfer(context, id + "F19", {"entities" : qUnion([Q0, Q1, Q2, Q3]), "width" : 1.6 * mm, "tangentPropagation" : true});
        }
        {
            var Q0;
            Q0=makeQuery(id+"F18.opExtrude","SWEPT_EDGE",EDGE,{"disambiguationData":[OSD([sQuery(id+"F17.wireOp",EDGE,"E64.MirrorCS"),sQuery(id+"F17.wireOp",EDGE,"E65.MirrorCS")])]});
            var Q1;
            Q1=makeQuery(id+"F18.opExtrude","SWEPT_EDGE",EDGE,{"disambiguationData":[OSD([sQuery(id+"F17.wireOp",EDGE,"E65.MirrorCS"),sQuery(id+"F17.wireOp",EDGE,"E66.MirrorCS")])]});
            var Q2;
            Q2=makeQuery(id+"F18.opExtrude","SWEPT_EDGE",EDGE,{"disambiguationData":[OSD([sQuery(id+"F17.wireOp",EDGE,"E54"),sQuery(id+"F17.wireOp",EDGE,"E66.MirrorCS")])]});
            var Q3;
            Q3=makeQuery(id+"F18.opExtrude","SWEPT_EDGE",EDGE,{"disambiguationData":[OSD([sQuery(id+"F17.wireOp",EDGE,"E45"),sQuery(id+"F17.wireOp",EDGE,"E63")])]});
            var Q4;
            Q4=makeQuery(id+"F18.opExtrude","SWEPT_EDGE",EDGE,{"disambiguationData":[OSD([sQuery(id+"F17.wireOp",EDGE,"E61"),sQuery(id+"F17.wireOp",EDGE,"E62")])]});
            var Q5;
            Q5=makeQuery(id+"F18.opExtrude","SWEPT_EDGE",EDGE,{"disambiguationData":[OSD([sQuery(id+"F17.wireOp",EDGE,"E62"),sQuery(id+"F17.wireOp",EDGE,"E63")])]});
            chamfer(context, id + "F20", {"entities" : qUnion([Q0, Q1, Q2, Q3, Q4, Q5]), "width" : .6 * mm, "tangentPropagation" : true});
        }
    });
